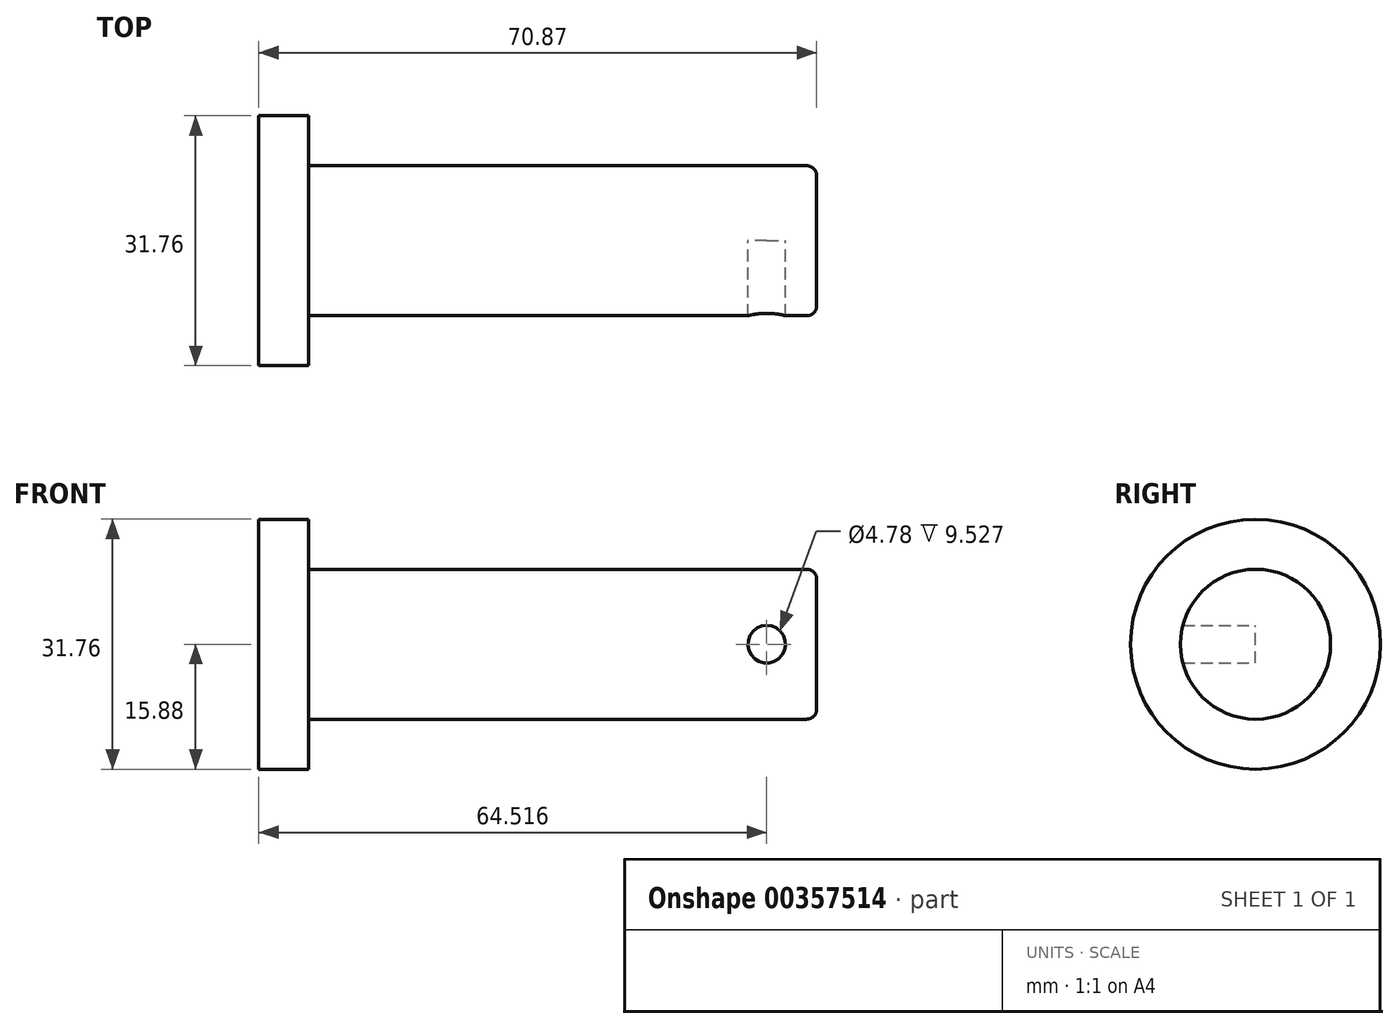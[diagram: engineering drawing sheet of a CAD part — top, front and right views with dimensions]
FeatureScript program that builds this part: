
annotation { "Feature Type Name" : "Feature", "Feature Type Description" : "" }
export const myFeature = defineFeature(function(context is Context, id is Id, definition is map)
    precondition{}
    {
        {
            var Q0;
            Q0=qCreatedBy(makeId("Right.planeOp"),FACE);
            var sketch = newSketch(context, id + "F0", { "sketchPlane" : qUnion([Q0])});
            skCircle(sketch, "E0", {"center": v(0, 0) * mm, "radius": 9.53 * mm});
            skSolve(sketch);
        }
        {
            var Q0;
            Q0 = qSketchRegion(id + "F0", true);
            extrude(context, id + "F1", {"entities" : qUnion([Q0]), "depth" : 64.52 * mm});
        }
        {
            var Q0;
            Q0=qCreatedBy(makeId("Front.planeOp"),FACE);
            var sketch = newSketch(context, id + "F2", { "sketchPlane" : qUnion([Q0])});
            skCircle(sketch, "E1", {"center": v(58.17, 0) * mm, "radius": 2.39 * mm});
            skSolve(sketch);
        }
        {
            var Q0;
            Q0=makeQuery(id+"F1.opExtrude","CAP_FACE",FACE,{"disambiguationData":[OSD([sQuery(id+"F0.wireOp",EDGE,"E0")])],"isStart":true});
            var sketch = newSketch(context, id + "F3", { "sketchPlane" : qUnion([Q0])});
            skCircle(sketch, "E2", {"center": v(0, 0) * mm, "radius": 15.88 * mm});
            skSolve(sketch);
        }
        {
            var Q0;
            Q0 = qSketchRegion(id + "F3", true);
            extrude(context, id + "F4", {"entities" : qUnion([Q0]), "operationType" : NewBodyOperationType.ADD, "depth" : 6.35 * mm});
        }
        {
            var Q0;
            Q0 = qSketchRegion(id + "F2", true);
            extrude(context, id + "F5", {"entities" : qUnion([Q0]), "operationType" : NewBodyOperationType.REMOVE, "endBound" : BoundingType.THROUGH_ALL, "depth" : 25.4 * mm});
        }
        {
            var Q0;
            Q0=makeQuery(id+"F1.opExtrude","CAP_FACE",FACE,{"disambiguationData":[OSD([sQuery(id+"F0.wireOp",EDGE,"E0")])],"isStart":false});
            fillet(context, id + "F6", {"entities" : qUnion([Q0]), "radius" : 1.27 * mm, "tangentPropagation" : true, "allowEdgeOverflow" : false});
        }
    });
